# Revit family: Gira_236500
name_source: partatom
category: Elektroinstallationen
revit_build: Autodesk Revit 2017 (Build: 20160225_1515(x64)
units: mm (PartAtom-declared; Revit-internal decimal feet)

## family parameters
Basisbauteil = Fläche
Beim Laden mit Abzugskörper schneiden = Nein
Bemaßung runder Anschluss = Durchmesser verwenden
Beschriftungsausrichtung beibehalten = Nein
Gemeinsam genutzt = Nein
Raumberechnungspunkt = Nein
Teiletyp = Normal

## types (1)
- S3000 Uni-LED-Dimmer REG Elektronik
    Anschlussart = Schraubklemme
    Anzahl der Eingänge = 0
    App-Steuerung über Bluetooth = Nein
    BIM = https://media.stage.bim.site X1 REG KNX.rfa
    BIMSITE_PRODUCT_ID = 8f91fb907f181f1ec18f10e8b15fd6913afbe936
    Bedienungsart = sonstige
    Befestigungsart = Klickbefestigung
    Beschreibung = System 3000 Universal-LED-Dimmer REG  REG Merkmale:  Schalten und Dimmen von Glühlampen, HV-Halogenlampen, elektronischen Trafos für Halogen- oder LED-Lampen, dimmbaren induktiven Trafos für Halogen- oder LED-Lampen, HV-LED- oder Kompaktleuchtstofflampen.  Schalten und Dimmen von Glühlampen, HV-Halogenlampen, elektronischen Trafos für Halogen- oder LED-Lampen, dimmbaren induktiven Trafos für Halogen- oder LED-Lampen, HV-LED- oder Kompaktleuchtstofflampen.  Bedienung erfolgt über mechanischen Taster (Schließer), System 3000 Nebenstelle 2- oder 3-Draht, oder System 2000 Nebenstelle 2-Draht.  Automatische oder manuelle Einstellung des zur Last passenden Dimmprinzips (Phasenan- oder Phasenabschnitt).  Anzeige der eingestellten Betriebsart mittels LED.  Lampenschonendes Einschalten.  Einschalthelligkeit dauerhaft speicherbar (mit System 2000 und 3000 Nebenstelle möglich).  Einschalten mit zuletzt eingestellter Helligkeit oder gespeicherter Einschalthelligkeit.  Minimalhelligkeit einstellbar.  Elektronischer Kurzschlussschutz.  Elektronischer Übertemperaturschutz.  Betrieb mit Neutralleiteranschluss.  Hinweise :  Bei höherer Umgebungstemperatur als 45 C ist die angeschlossene Last zu reduzieren.
    Breite in Teilungseinheiten = 0
    Bussystem Funkbus = Nein
    Bussystem KNX = Nein
    Bussystem KNX-Funk = Nein
    Bussystem LON = Nein
    Bussystem Powernet = Nein
    Datenblatt = https://media.stage.bim.site
    Datenblatt 1 = https://media.stage.bim.site
    Dimmung Phasenabschnitt = Nein
    Dimmung Phasenanschnitt = Nein
    Frequenz [Hz] = [50:60]
    Funk bidirektional = Nein
    Funktion Schalten = Nein
    GTIN = 4010337031376
    Geeignet für Schutzart (IP) = IP20
    HAN = 236500
    Halogenfrei = Nein
    HeinzeBIM = https://www.heinze.de
    Hersteller = Gira
    Kosten = 0 $
    Lastart = universal und LED Retrofit
    Lichtwertspeicher = Nein
    Max. Anzahl der Jalousieausgänge = 0
    Max. Schaltleistung [Voltampere] = 0
    Mit Beschriftungsfeld = Nein
    Mit Busankopplung = Nein
    Mit LED-Anzeige = Nein
    Montageart = REG
    Nebenstelleneingang = Ja
    Nennspannung [Volt] = [230:230]
    Oberfläche Text = sonstige
    Produktseite = https://media.stage.bim.site
    Seriendimmer = Nein
    Transparent = Nein
    Typname = S3000 Uni-LED-Dimmer REG Elektronik
    URL = https://www.gira.de
    Verwendbar mit Bewegungsmelder = Ja
    Verwendbar mit Funktaste = Nein
    Verwendbar mit IR-Taste = Nein
    Verwendbar mit Präsenzmelder = Ja
    Verwendbar mit Taste = Ja
    Verwendbar mit Zeitschalter/Timer = Nein
    Vor Ort-/Handbedienung = Nein
    Vorgabe-Ansicht = 1219 mm
    Werkstoff Text = sonstige
    Werkstoffgüte = sonstige
    Zusammenstellung = Basiselement mit Komplettgehäuse

## geometry (parser evidence)
native form markers: Sweep x2
no freeform markers — native parametric forms only
